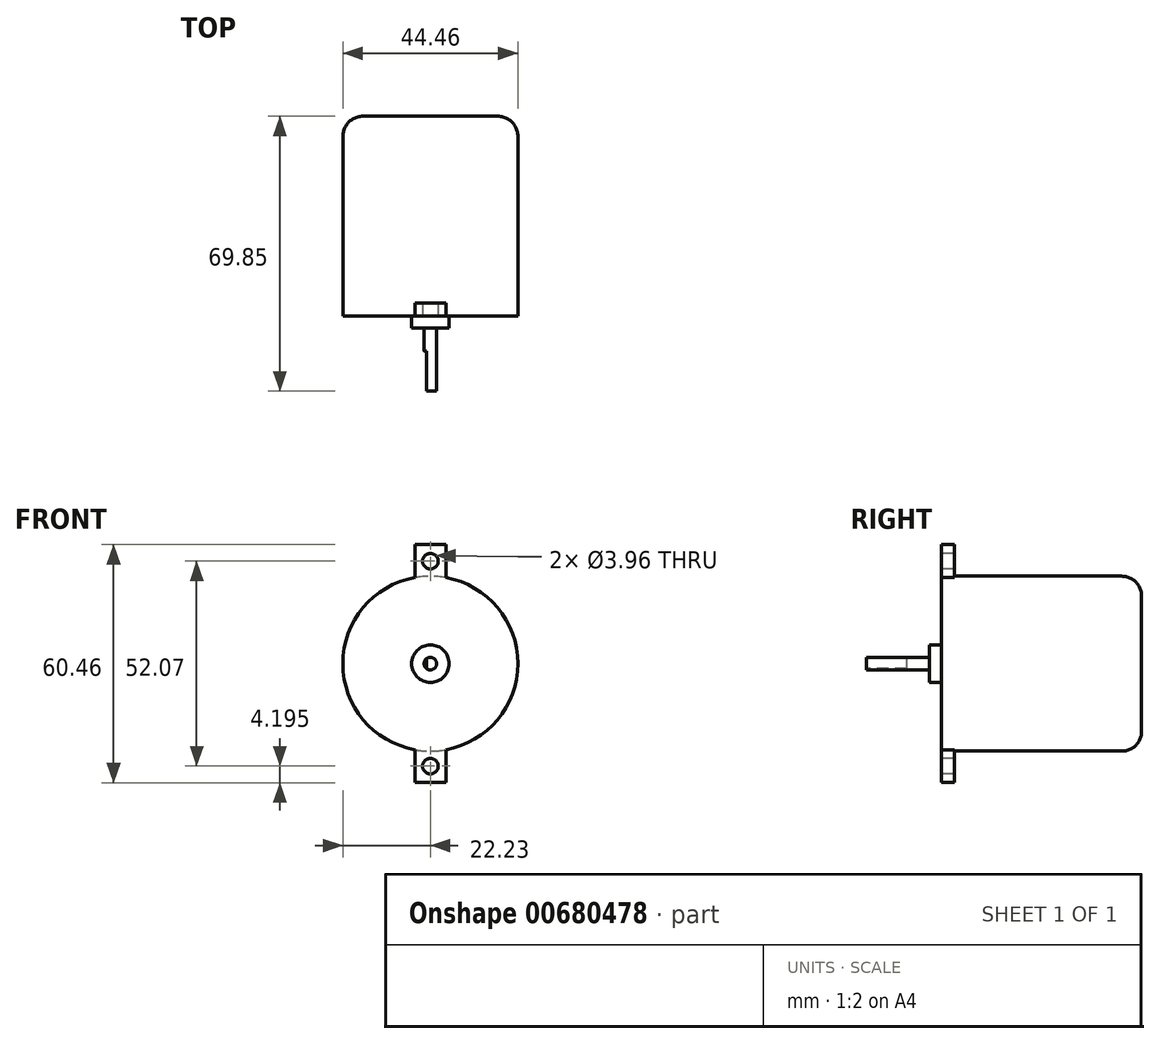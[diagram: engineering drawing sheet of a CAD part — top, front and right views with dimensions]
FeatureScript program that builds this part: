
annotation { "Feature Type Name" : "Feature", "Feature Type Description" : "" }
export const myFeature = defineFeature(function(context is Context, id is Id, definition is map)
    precondition{}
    {
        {
            var Q0;
            Q0=qCreatedBy(makeId("Front.planeOp"),FACE);
            var sketch = newSketch(context, id + "F0", { "sketchPlane" : qUnion([Q0])});
            skCircle(sketch, "E0", {"center": v(0, 0) * mm, "radius": 22.23 * mm});
            skSolve(sketch);
        }
        {
            var Q0;
            Q0=makeQuery(id+"F0.imprint","IMPRINT",FACE,{"disambiguationData":[TD([[makeQuery(id+"F0.imprint","IMPRINT",EDGE,{"derivedFrom":sQuery(id+"F0.wireOp",EDGE,"E0")}),1.0]])]});
            extrude(context, id + "F1", {"entities" : qUnion([Q0]), "depth" : 50.8 * mm, "offsetDistance" : 25.4 * mm});
        }
        {
            var Q0;
            Q0=makeQuery(id+"F1.opExtrude","CAP_FACE",FACE,{"disambiguationData":[OSD([sQuery(id+"F0.wireOp",EDGE,"E0")])],"isStart":false});
            var sketch = newSketch(context, id + "F2", { "sketchPlane" : qUnion([Q0])});
            skCircle(sketch, "E1", {"center": v(0, 0) * mm, "radius": 4.76 * mm});
            skSolve(sketch);
        }
        {
            var Q0;
            Q0=makeQuery(id+"F2.imprint","IMPRINT",FACE,{"disambiguationData":[TD([[makeQuery(id+"F2.imprint","IMPRINT",EDGE,{"derivedFrom":sQuery(id+"F2.wireOp",EDGE,"E1")}),1.0]])]});
            extrude(context, id + "F3", {"entities" : qUnion([Q0]), "operationType" : NewBodyOperationType.ADD, "depth" : 19.05 * mm - 16 * mm, "offsetDistance" : 25.4 * mm});
        }
        {
            var Q0;
            Q0=makeQuery(id+"F3.opExtrude","CAP_FACE",FACE,{"disambiguationData":[OSD([sQuery(id+"F2.wireOp",EDGE,"E1")])],"isStart":false});
            var sketch = newSketch(context, id + "F4", { "sketchPlane" : qUnion([Q0])});
            skCircle(sketch, "E2", {"center": v(0, 0) * mm, "radius": 1.59 * mm});
            skSolve(sketch);
        }
        {
            var Q0;
            Q0=makeQuery(id+"F4.imprint","IMPRINT",FACE,{"disambiguationData":[TD([[makeQuery(id+"F4.imprint","IMPRINT",EDGE,{"derivedFrom":sQuery(id+"F4.wireOp",EDGE,"E2")}),1.0]])]});
            extrude(context, id + "F5", {"entities" : qUnion([Q0]), "operationType" : NewBodyOperationType.ADD, "depth" : 16 * mm, "offsetDistance" : 25.4 * mm});
        }
        {
            var Q0;
            Q0=makeQuery(id+"F5.opExtrude","CAP_FACE",FACE,{"disambiguationData":[OSD([sQuery(id+"F4.wireOp",EDGE,"E2")])],"isStart":false});
            var sketch = newSketch(context, id + "F6", { "sketchPlane" : qUnion([Q0])});
            skLineSegment(sketch, "E3", {"start": v(-0.95, 1.27) * mm, "end": v(-0.95, -1.27) * mm});
            skArc(sketch, "E4.0", {"start": v(-0.95, 1.27) * mm, "mid": v(-1.59, 0) * mm, "end": v(-0.95, -1.27) * mm});
            skPoint(sketch, "E5", {"position": v(1.59, 0) * mm});
            skSolve(sketch);
        }
        {
            var Q0;
            Q0=makeQuery(id+"F6.imprint","IMPRINT",FACE,{"disambiguationData":[TD([[makeQuery(id+"F6.imprint","IMPRINT",EDGE,{"derivedFrom":sQuery(id+"F6.wireOp",EDGE,"E3")}),-1.0]])]});
            extrude(context, id + "F7", {"entities" : qUnion([Q0]), "operationType" : NewBodyOperationType.REMOVE, "oppositeDirection" : true, "depth" : 10.16 * mm, "offsetDistance" : 25.4 * mm});
        }
        {
            var Q0;
            Q0=makeQuery(id+"F1.opExtrude","CAP_EDGE",EDGE,{"disambiguationData":[OSD([sQuery(id+"F0.wireOp",EDGE,"E0")])],"isStart":true});
            fillet(context, id + "F8", {"entities" : qUnion([Q0]), "radius" : 5.08 * mm, "tangentPropagation" : true, "allowEdgeOverflow" : false});
        }
        {
            var Q0;
            Q0=makeQuery(id+"F1.opExtrude","CAP_FACE",FACE,{"disambiguationData":[OSD([sQuery(id+"F0.wireOp",EDGE,"E0")])],"isStart":false});
            var sketch = newSketch(context, id + "F9", { "sketchPlane" : qUnion([Q0])});
            skLineSegment(sketch, "E6.bottom", {"start": v(3.94, 30.23) * mm, "end": v(-3.94, 30.23) * mm});
            skLineSegment(sketch, "E6.top", {"start": v(3.94, -30.23) * mm, "end": v(-3.94, -30.23) * mm});
            skLineSegment(sketch, "E6.left", {"start": v(3.94, 30.23) * mm, "end": v(3.94, -30.23) * mm});
            skLineSegment(sketch, "E6.right", {"start": v(-3.94, 30.23) * mm, "end": v(-3.94, -30.23) * mm});
            skPoint(sketch, "E6.middle", {"position": v(0, 0) * mm});
            skSolve(sketch);
        }
        {
            var Q0;
            {var subQ0=sQuery(id+"F9.wireOp",EDGE,"E6.bottom");Q0=makeQuery(id+"F9.imprint","IMPRINT",FACE,{"disambiguationData":[TD([[makeQuery(id+"F9.imprint","IMPRINT",EDGE,{"derivedFrom":subQ0}),1.0]])]});}
            var Q1;
            {var subQ0=sQuery(id+"F9.wireOp",EDGE,"E6.top");Q1=makeQuery(id+"F9.imprint","IMPRINT",FACE,{"disambiguationData":[TD([[makeQuery(id+"F9.imprint","IMPRINT",EDGE,{"derivedFrom":subQ0}),-1.0]])]});}
            extrude(context, id + "F10", {"entities" : qUnion([Q0, Q1]), "operationType" : NewBodyOperationType.ADD, "oppositeDirection" : true, "depth" : 3.3 * mm, "offsetDistance" : 25.4 * mm});
        }
        {
            var Q0;
            {var subQ0=sQuery(id+"F9.wireOp",EDGE,"E6.right");var subQ1=sQuery(id+"F9.wireOp",EDGE,"E6.left");var subQ2=sQuery(id+"F0.wireOp",EDGE,"E0");Q0=makeQuery(id+"F10.boolean.opBoolean","MERGE",FACE,{"derivedFrom":[makeQuery(id+"F1.opExtrude","CAP_FACE",FACE,{"disambiguationData":[OSD([subQ2])],"isStart":false}),makeQuery(id+"F10.opExtrude","CAP_FACE",FACE,{"disambiguationData":[OSD([subQ2,sQuery(id+"F9.wireOp",EDGE,"E6.bottom"),subQ1,subQ0])],"isStart":true}),makeQuery(id+"F10.opExtrude","CAP_FACE",FACE,{"disambiguationData":[OSD([subQ2,sQuery(id+"F9.wireOp",EDGE,"E6.top"),subQ1,subQ0])],"isStart":true})]});}
            var sketch = newSketch(context, id + "F11", { "sketchPlane" : qUnion([Q0])});
            skCircle(sketch, "E7", {"center": v(0, 26.04) * mm, "radius": 1.98 * mm});
            skCircle(sketch, "E8", {"center": v(0, -26.04) * mm, "radius": 1.98 * mm});
            skLineSegment(sketch, "E9", {"start": v(0, 0) * mm, "end": v(0, 26.04) * mm, "construction": true});
            skLineSegment(sketch, "E10", {"start": v(0, 0) * mm, "end": v(0, -26.04) * mm, "construction": true});
            skSolve(sketch);
        }
        {
            var Q0;
            Q0=makeQuery(id+"F11.imprint","IMPRINT",FACE,{"disambiguationData":[TD([[makeQuery(id+"F11.imprint","IMPRINT",EDGE,{"derivedFrom":sQuery(id+"F11.wireOp",EDGE,"E7")}),1.0]])]});
            var Q1;
            Q1=makeQuery(id+"F11.imprint","IMPRINT",FACE,{"disambiguationData":[TD([[makeQuery(id+"F11.imprint","IMPRINT",EDGE,{"derivedFrom":sQuery(id+"F11.wireOp",EDGE,"E8")}),1.0]])]});
            extrude(context, id + "F12", {"entities" : qUnion([Q0, Q1]), "operationType" : NewBodyOperationType.REMOVE, "endBound" : BoundingType.THROUGH_ALL, "oppositeDirection" : true, "depth" : 25.4 * mm, "offsetDistance" : 25.4 * mm});
        }
    });
